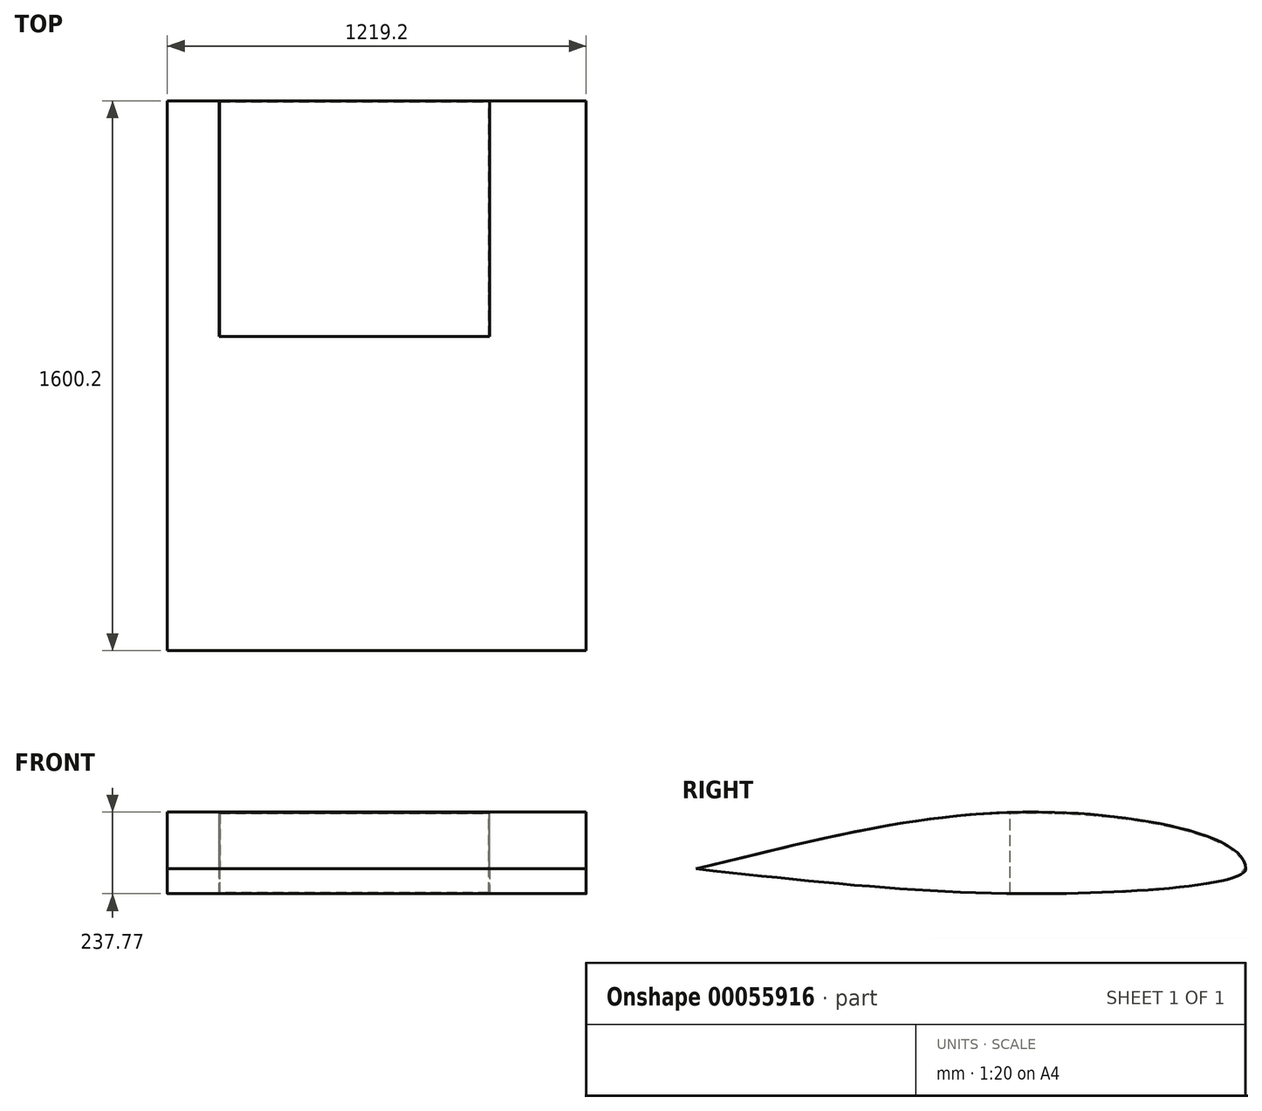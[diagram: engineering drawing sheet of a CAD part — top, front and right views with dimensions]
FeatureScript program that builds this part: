
annotation { "Feature Type Name" : "Feature", "Feature Type Description" : "" }
export const myFeature = defineFeature(function(context is Context, id is Id, definition is map)
    precondition{}
    {
        {
            var Q0;
            Q0=qCreatedBy(makeId("Right.planeOp"),FACE);
            var sketch = newSketch(context, id + "F0", { "sketchPlane" : qUnion([Q0])});
            skLineSegment(sketch, "E0", {"start": v(0, 0) * mm, "end": v(-1600.2, 0) * mm});
            skLineSegment(sketch, "E1", {"start": v(-557.27, 0) * mm, "end": v(-557.27, 164.5) * mm});
            skFitSpline(sketch, "E2", {"points": [v(0, 0) * mm, v(-557.27, 164.5) * mm, v(-1600.2, 0) * mm], "startDerivative": vector(0, 679.45) * mm, "endDerivative": vector(-1962.48, -479.66) * mm});
            skLineSegment(sketch, "E3", {"start": v(-557.27, 0) * mm, "end": v(-557.27, -72) * mm});
            skFitSpline(sketch, "E4", {"points": [v(0, 0) * mm, v(-557.27, -72) * mm, v(-1600.2, 0) * mm], "startDerivative": vector(0, -318.03) * mm, "endDerivative": vector(-1948.95, 209.92) * mm});
            skSolve(sketch);
        }
        {
            var Q0;
            {var subQ3=sQuery(id+"F0.wireOp",EDGE,"E1");Q0=makeQuery(id+"F0.imprint","IMPRINT",FACE,{"disambiguationData":[TD([[makeQuery(id+"F0.imprint","IMPRINT",EDGE,{"derivedFrom":subQ3}),1.0]])]});}
            var Q1;
            {var subQ3=sQuery(id+"F0.wireOp",EDGE,"E1");Q1=makeQuery(id+"F0.imprint","IMPRINT",FACE,{"disambiguationData":[TD([[makeQuery(id+"F0.imprint","IMPRINT",EDGE,{"derivedFrom":subQ3}),-1.0]])]});}
            var Q2;
            {var subQ3=sQuery(id+"F0.wireOp",EDGE,"E3");Q2=makeQuery(id+"F0.imprint","IMPRINT",FACE,{"disambiguationData":[TD([[makeQuery(id+"F0.imprint","IMPRINT",EDGE,{"derivedFrom":subQ3}),1.0]])]});}
            var Q3;
            {var subQ3=sQuery(id+"F0.wireOp",EDGE,"E3");Q3=makeQuery(id+"F0.imprint","IMPRINT",FACE,{"disambiguationData":[TD([[makeQuery(id+"F0.imprint","IMPRINT",EDGE,{"derivedFrom":subQ3}),-1.0]])]});}
            extrude(context, id + "F1", {"entities" : qUnion([Q0, Q1, Q2, Q3]), "depth" : 1219.2 * mm});
        }
        {
            var Q0;
            Q0=qCreatedBy(makeId("Top.planeOp"),FACE);
            var sketch = newSketch(context, id + "F2", { "sketchPlane" : qUnion([Q0])});
            skLineSegment(sketch, "E5.bottom", {"start": v(152.4, 0) * mm, "end": v(937.51, 0) * mm});
            skLineSegment(sketch, "E5.top", {"start": v(152.4, -685.8) * mm, "end": v(937.51, -685.8) * mm});
            skLineSegment(sketch, "E5.left", {"start": v(152.4, 0) * mm, "end": v(152.4, -685.8) * mm});
            skLineSegment(sketch, "E5.right", {"start": v(937.51, 0) * mm, "end": v(937.51, -685.8) * mm});
            skSolve(sketch);
        }
        {
            var Q0;
            Q0 = qSketchRegion(id + "F2", true);
            extrude(context, id + "F3", {"entities" : qUnion([Q0]), "operationType" : NewBodyOperationType.REMOVE, "endBound" : BoundingType.THROUGH_ALL, "oppositeDirection" : true, "depth" : 25.4 * mm, "hasSecondDirection" : true, "secondDirectionBound" : SecondDirectionBoundingType.THROUGH_ALL, "secondDirectionOppositeDirection" : false, "secondDirectionDepth" : 25.4 * mm});
        }
        {
            var Q0;
            Q0=makeQuery(id+"F3.boolean.opBoolean","COPY",FACE,{"derivedFrom":makeQuery(id+"F3.opExtrude","SWEPT_FACE",FACE,{"disambiguationData":[OSD([sQuery(id+"F2.wireOp",EDGE,"E5.right")])]})});
            var sketch = newSketch(context, id + "F4", { "sketchPlane" : qUnion([Q0])});
            skFitSpline(sketch, "E6.0", {"points": [v(685.6, 158.08) * mm, v(666.9, 158.66) * mm, v(638.68, 159.17) * mm, v(600.72, 159.08) * mm, v(576.83, 158.69) * mm, v(557.62, 158.18) * mm, v(538.34, 157.52) * mm, v(514.14, 156.46) * mm, v(485.02, 154.77) * mm, v(446.22, 151.99) * mm, v(398, 147.52) * mm, v(341.33, 140.61) * mm, v(286.59, 132.2) * mm, v(234.52, 122.32) * mm, v(185.88, 111.02) * mm, v(141.43, 98.34) * mm, v(101.91, 84.34) * mm, v(68.12, 69.1) * mm, v(45.4, 55.47) * mm, v(30.88, 44.14) * mm, v(21.9, 35.47) * mm, v(14.93, 26.7) * mm, v(9.97, 17.87) * mm, v(7.02, 9.02) * mm, v(6.35, 3.04) * mm, v(6.35, 0) * mm], "construction": true});
            skLineSegment(sketch, "E6.1", {"start": v(679.45, -65.52) * mm, "end": v(679.45, 158.26) * mm, "construction": true});
            skFitSpline(sketch, "E6.2", {"points": [v(685.7, -65.44) * mm, v(667.08, -65.7) * mm, v(638.97, -65.96) * mm, v(601.1, -65.98) * mm, v(577.27, -65.86) * mm, v(558.09, -65.67) * mm, v(538.84, -65.44) * mm, v(514.65, -65.03) * mm, v(485.54, -64.38) * mm, v(446.74, -63.28) * mm, v(398.47, -61.5) * mm, v(341.69, -58.67) * mm, v(286.79, -55.18) * mm, v(234.52, -51.03) * mm, v(185.64, -46.2) * mm, v(140.9, -40.72) * mm, v(107.7, -35.61) * mm, v(83.98, -31.2) * mm, v(67.71, -27.75) * mm, v(53.07, -24.14) * mm, v(40.17, -20.4) * mm, v(29.13, -16.53) * mm, v(20.09, -12.58) * mm, v(14.35, -9.3) * mm, v(10.93, -6.78) * mm, v(8.97, -5) * mm, v(7.6, -3.38) * mm, v(6.8, -2.01) * mm, v(6.42, -0.92) * mm, v(6.35, -0.31) * mm, v(6.35, 0) * mm], "construction": true});
            skSolve(sketch);
        }
        {
            var Q0;
            {var subQ0=sQuery(id+"F2.wireOp",EDGE,"E5.right");Q0=makeQuery(id+"F4.imprint","IMPRINT",FACE,{"disambiguationData":[TD([[makeQuery(id+"F4.imprint","IMPRINT",EDGE,{"derivedFrom":makeQuery(id+"F3.boolean.opBoolean","COPY",EDGE,{"derivedFrom":makeQuery(id+"F3.opExtrude","SWEPT_EDGE",EDGE,{"disambiguationData":[OSD([sQuery(id+"F2.wireOp",EDGE,"E5.top"),subQ0])]})})}),1.0]])]});}
            extrude(context, id + "F5", {"entities" : qUnion([Q0]), "depth" : 787.4 * mm});
        }
        {
            var Q0;
            Q0=makeQuery(id+"F5.opExtrude","SWEPT_FACE",FACE,{"disambiguationData":[OSD([sQuery(id+"F2.wireOp",EDGE,"E5.top"),sQuery(id+"F2.wireOp",EDGE,"E5.right")])]});
            shell(context, id + "F6", {"entities" : qUnion([Q0]), "thickness" : 2.54 * mm});
        }
    });
